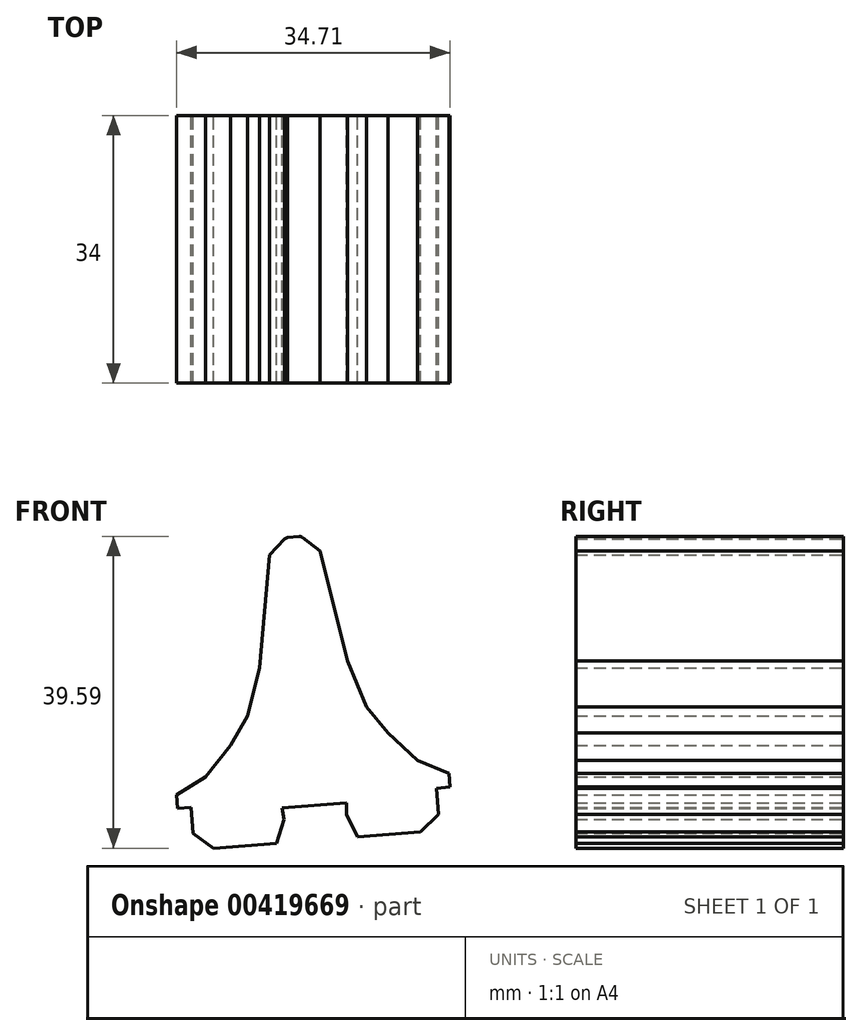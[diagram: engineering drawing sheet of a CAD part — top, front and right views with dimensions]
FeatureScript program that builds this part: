
annotation { "Feature Type Name" : "Feature", "Feature Type Description" : "" }
export const myFeature = defineFeature(function(context is Context, id is Id, definition is map)
    precondition{}
    {
        {
            var Q0;
            Q0=qCreatedBy(makeId("Front.planeOp"),FACE);
            var sketch = newSketch(context, id + "F0", { "sketchPlane" : qUnion([Q0])});
            skLineSegment(sketch, "E0", {"start": v(-12.43, -12.85) * mm, "end": v(-4.22, -12.2) * mm});
            skLineSegment(sketch, "E1", {"start": v(-11, 21.53) * mm, "end": v(-7.52, -22.76) * mm, "construction": true});
            skPoint(sketch, "E2", {"position": v(-8.32, -12.53) * mm});
            skLineSegment(sketch, "E3", {"start": v(-11, 21.56) * mm, "end": v(-10.27, 21.62) * mm});
            skLineSegment(sketch, "E4", {"start": v(-9.83, 21.49) * mm, "end": v(-7.63, 19.8) * mm});
            skLineSegment(sketch, "E5", {"start": v(-7.63, 19.8) * mm, "end": v(-4.14, 5.8) * mm});
            skLineSegment(sketch, "E6", {"start": v(-4.14, 5.8) * mm, "end": v(-1.72, 0) * mm});
            skLineSegment(sketch, "E7", {"start": v(-1.72, 0) * mm, "end": v(1, -3.35) * mm});
            skLineSegment(sketch, "E8", {"start": v(1, -3.35) * mm, "end": v(4.79, -6.83) * mm});
            skLineSegment(sketch, "E9", {"start": v(4.79, -6.83) * mm, "end": v(8.75, -8.47) * mm});
            skLineSegment(sketch, "E10", {"start": v(8.75, -8.47) * mm, "end": v(8.89, -10.22) * mm});
            skLineSegment(sketch, "E11", {"start": v(8.89, -10.22) * mm, "end": v(7.18, -10.35) * mm});
            skLineSegment(sketch, "E12", {"start": v(7.18, -10.35) * mm, "end": v(7.44, -13.68) * mm});
            skLineSegment(sketch, "E13", {"start": v(7.44, -13.68) * mm, "end": v(5.17, -15.9) * mm});
            skLineSegment(sketch, "E14", {"start": v(5.17, -15.9) * mm, "end": v(-2.82, -16.53) * mm});
            skLineSegment(sketch, "E15", {"start": v(-2.82, -16.53) * mm, "end": v(-4.22, -13.68) * mm});
            skLineSegment(sketch, "E16", {"start": v(-4.22, -13.68) * mm, "end": v(-4.22, -12.2) * mm});
            skPoint(sketch, "E17.visualSharp", {"position": v(-10.02, 21.64) * mm});
            skArc(sketch, "E17.filletArc", {"start": v(-9.83, 21.49) * mm, "mid": v(-10.04, 21.6) * mm, "end": v(-10.27, 21.62) * mm});
            skLineSegment(sketch, "E18.MirrorCS", {"start": v(-4.22, -12.2) * mm, "end": v(-12.43, -12.85) * mm});
            skLineSegment(sketch, "E19.MirrorCS", {"start": v(-12.2, -14.3) * mm, "end": v(-12.43, -12.85) * mm});
            skLineSegment(sketch, "E20.MirrorCS", {"start": v(-21.12, -17.97) * mm, "end": v(-13.14, -17.34) * mm});
            skLineSegment(sketch, "E21.MirrorCS", {"start": v(-13.14, -17.34) * mm, "end": v(-12.2, -14.3) * mm});
            skLineSegment(sketch, "E22.MirrorCS", {"start": v(-23.72, -16.12) * mm, "end": v(-21.12, -17.97) * mm});
            skLineSegment(sketch, "E23.MirrorCS", {"start": v(-23.98, -12.8) * mm, "end": v(-23.72, -16.12) * mm});
            skLineSegment(sketch, "E24.MirrorCS", {"start": v(-25.68, -12.93) * mm, "end": v(-23.98, -12.8) * mm});
            skLineSegment(sketch, "E25.MirrorCS", {"start": v(-25.82, -11.18) * mm, "end": v(-25.68, -12.93) * mm});
            skLineSegment(sketch, "E26.MirrorCS", {"start": v(-22.17, -8.94) * mm, "end": v(-25.82, -11.18) * mm});
            skLineSegment(sketch, "E27.MirrorCS", {"start": v(-18.97, -4.92) * mm, "end": v(-22.17, -8.94) * mm});
            skLineSegment(sketch, "E28.MirrorCS", {"start": v(-16.8, -1.18) * mm, "end": v(-18.97, -4.92) * mm});
            skLineSegment(sketch, "E29.MirrorCS", {"start": v(-15.32, 4.93) * mm, "end": v(-16.8, -1.18) * mm});
            skLineSegment(sketch, "E30.MirrorCS", {"start": v(-14.04, 19.3) * mm, "end": v(-15.32, 4.93) * mm});
            skLineSegment(sketch, "E31.MirrorCS", {"start": v(-12.14, 21.3) * mm, "end": v(-14.04, 19.3) * mm});
            skLineSegment(sketch, "E32.MirrorCS", {"start": v(-11, 21.56) * mm, "end": v(-11.73, 21.5) * mm});
            skLineSegment(sketch, "E33", {"start": v(-12.14, 21.3) * mm, "end": v(-11.73, 21.5) * mm});
            skSolve(sketch);
        }
        {
            var Q0;
            Q0=makeQuery(id+"F0.imprint","IMPRINT",FACE,{"disambiguationData":[TD([[makeQuery(id+"F0.imprint","IMPRINT",EDGE,{"derivedFrom":sQuery(id+"F0.wireOp",EDGE,"E3")}),-1.0]])]});
            extrude(context, id + "F1", {"entities" : qUnion([Q0]), "depth" : 34 * mm});
        }
    });
